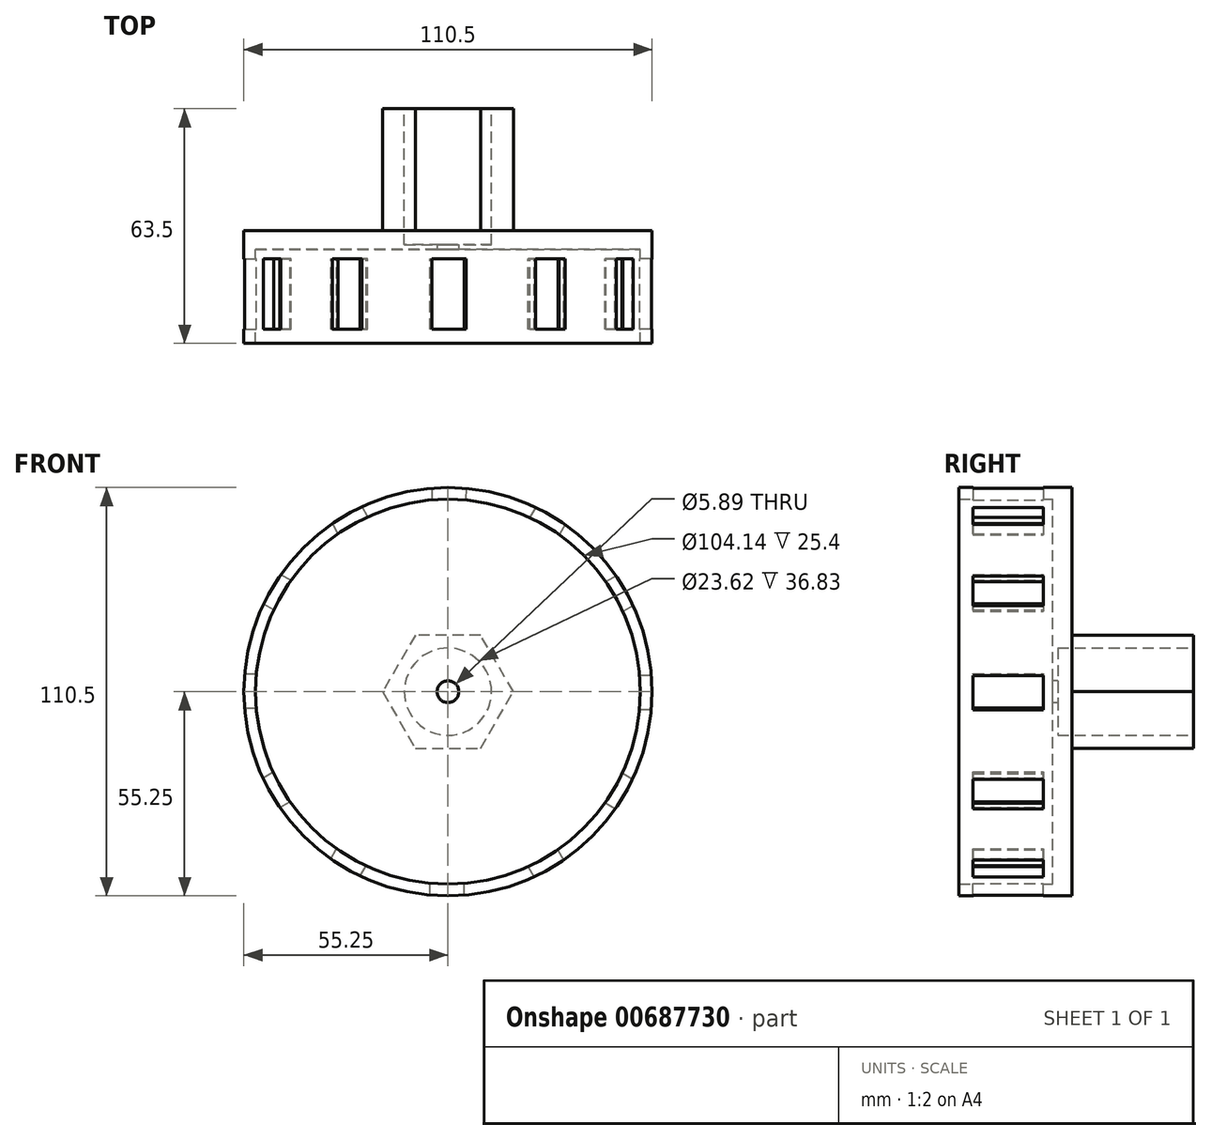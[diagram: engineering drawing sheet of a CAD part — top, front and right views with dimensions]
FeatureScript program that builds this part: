
annotation { "Feature Type Name" : "Feature", "Feature Type Description" : "" }
export const myFeature = defineFeature(function(context is Context, id is Id, definition is map)
    precondition{}
    {
        {
            var Q0;
            Q0=qCreatedBy(makeId("Front.planeOp"),FACE);
            var sketch = newSketch(context, id + "F0", { "sketchPlane" : qUnion([Q0])});
            skCircle(sketch, "E0", {"center": v(0, 0) * mm, "radius": 52.07 * mm});
            skCircle(sketch, "E1", {"center": v(0, 0) * mm, "radius": 55.24 * mm});
            skSolve(sketch);
        }
        {
            var Q0;
            Q0=makeQuery(id+"F0.imprint","IMPRINT",FACE,{"disambiguationData":[TD([[makeQuery(id+"F0.imprint","IMPRINT",EDGE,{"derivedFrom":sQuery(id+"F0.wireOp",EDGE,"E0")}),1.0]])]});
            extrude(context, id + "F1", {"entities" : qUnion([Q0]), "depth" : 5.08 * mm, "offsetDistance" : 25.4 * mm});
        }
        {
            var Q0;
            Q0=makeQuery(id+"F0.imprint","IMPRINT",FACE,{"disambiguationData":[TD([[makeQuery(id+"F0.imprint","IMPRINT",EDGE,{"derivedFrom":sQuery(id+"F0.wireOp",EDGE,"E0")}),-1.0]])]});
            extrude(context, id + "F2", {"entities" : qUnion([Q0]), "operationType" : NewBodyOperationType.ADD, "depth" : 30.48 * mm, "offsetDistance" : 25.4 * mm});
        }
        {
            var Q0;
            Q0=makeQuery(id+"F1.opExtrude","CAP_FACE",FACE,{"disambiguationData":[OSD([sQuery(id+"F0.wireOp",EDGE,"E0")])],"isStart":false});
            var sketch = newSketch(context, id + "F3", { "sketchPlane" : qUnion([Q0])});
            skCircle(sketch, "E2.cCircle", {"center": v(0, 0) * mm, "radius": 17.26 * mm, "construction": true});
            skLineSegment(sketch, "E2.0", {"start": v(12.58, -12.7) * mm, "end": v(4.55, -17.28) * mm});
            skLineSegment(sketch, "E2.1", {"start": v(4.55, -17.28) * mm, "end": v(-4.7, -17.24) * mm});
            skLineSegment(sketch, "E2.2", {"start": v(-4.7, -17.24) * mm, "end": v(-12.7, -12.58) * mm});
            skLineSegment(sketch, "E2.3", {"start": v(-12.7, -12.58) * mm, "end": v(-17.28, -4.55) * mm});
            skLineSegment(sketch, "E2.4", {"start": v(-17.28, -4.55) * mm, "end": v(-17.24, 4.7) * mm});
            skLineSegment(sketch, "E2.5", {"start": v(-17.24, 4.7) * mm, "end": v(-12.58, 12.7) * mm});
            skLineSegment(sketch, "E2.6", {"start": v(-12.58, 12.7) * mm, "end": v(-4.55, 17.28) * mm});
            skLineSegment(sketch, "E2.7", {"start": v(-4.55, 17.28) * mm, "end": v(4.7, 17.24) * mm});
            skLineSegment(sketch, "E2.8", {"start": v(4.7, 17.24) * mm, "end": v(12.7, 12.58) * mm});
            skLineSegment(sketch, "E2.9", {"start": v(12.7, 12.58) * mm, "end": v(17.28, 4.55) * mm});
            skLineSegment(sketch, "E2.10", {"start": v(17.28, 4.55) * mm, "end": v(17.24, -4.7) * mm});
            skLineSegment(sketch, "E2.11", {"start": v(17.24, -4.7) * mm, "end": v(12.58, -12.7) * mm});
            skPoint(sketch, "E2.0.midPoint", {"position": v(8.57, -14.99) * mm});
            skSolve(sketch);
        }
        {
            var Q0;
            Q0=makeQuery(id+"F3.imprint","IMPRINT",FACE,{"disambiguationData":[TD([[makeQuery(id+"F3.imprint","IMPRINT",EDGE,{"derivedFrom":sQuery(id+"F3.wireOp",EDGE,"E2.0")}),-1.0]])]});
            extrude(context, id + "F4", {"entities" : qUnion([Q0]), "operationType" : NewBodyOperationType.ADD, "depth" : 21.59 * mm, "offsetDistance" : 25.4 * mm});
        }
        {
            var Q0;
            Q0=makeQuery(id+"F4.opExtrude","SWEPT_FACE",FACE,{"disambiguationData":[OSD([sQuery(id+"F3.wireOp",EDGE,"E2.8")])]});
            var sketch = newSketch(context, id + "F5", { "sketchPlane" : qUnion([Q0])});
            skLineSegment(sketch, "E3", {"start": v(-4.63, -7.62) * mm, "end": v(4.63, -7.62) * mm});
            skSolve(sketch);
        }
        {
            var Q0;
            {var subQ0=sQuery(id+"F5.wireOp",EDGE,"E3");Q0=makeQuery(id+"F5.imprint","IMPRINT",FACE,{"disambiguationData":[TD([[makeQuery(id+"F5.imprint","IMPRINT",EDGE,{"derivedFrom":subQ0}),-1.0]])]});}
            extrude(context, id + "F6", {"entities" : qUnion([Q0]), "operationType" : NewBodyOperationType.REMOVE, "depth" : 50.8 * mm, "offsetDistance" : 25.4 * mm});
        }
        {
            var Q0;
            Q0=makeQuery(id+"F4.opExtrude","SWEPT_FACE",FACE,{"disambiguationData":[OSD([sQuery(id+"F3.wireOp",EDGE,"E2.7")])]});
            var sketch = newSketch(context, id + "F7", { "sketchPlane" : qUnion([Q0])});
            skLineSegment(sketch, "E4", {"start": v(4.63, -7.62) * mm, "end": v(-4.63, -7.62) * mm});
            skSolve(sketch);
        }
        {
            var Q0;
            {var subQ0=sQuery(id+"F7.wireOp",EDGE,"E4");Q0=makeQuery(id+"F7.imprint","IMPRINT",FACE,{"disambiguationData":[TD([[makeQuery(id+"F7.imprint","IMPRINT",EDGE,{"derivedFrom":subQ0}),1.0]])]});}
            extrude(context, id + "F8", {"entities" : qUnion([Q0]), "operationType" : NewBodyOperationType.REMOVE, "depth" : 50.8 * mm, "offsetDistance" : 25.4 * mm});
        }
        {
            var Q0;
            Q0=makeQuery(id+"F4.opExtrude","SWEPT_FACE",FACE,{"disambiguationData":[OSD([sQuery(id+"F3.wireOp",EDGE,"E2.6")])]});
            var sketch = newSketch(context, id + "F9", { "sketchPlane" : qUnion([Q0])});
            skLineSegment(sketch, "E5", {"start": v(4.63, -7.62) * mm, "end": v(-4.63, -7.62) * mm});
            skSolve(sketch);
        }
        {
            var Q0;
            {var subQ0=sQuery(id+"F9.wireOp",EDGE,"E5");Q0=makeQuery(id+"F9.imprint","IMPRINT",FACE,{"disambiguationData":[TD([[makeQuery(id+"F9.imprint","IMPRINT",EDGE,{"derivedFrom":subQ0}),1.0]])]});}
            extrude(context, id + "F10", {"entities" : qUnion([Q0]), "operationType" : NewBodyOperationType.REMOVE, "depth" : 50.8 * mm, "offsetDistance" : 25.4 * mm});
        }
        {
            var Q0;
            Q0=makeQuery(id+"F4.opExtrude","SWEPT_FACE",FACE,{"disambiguationData":[OSD([sQuery(id+"F3.wireOp",EDGE,"E2.5")])]});
            var sketch = newSketch(context, id + "F11", { "sketchPlane" : qUnion([Q0])});
            skLineSegment(sketch, "E6", {"start": v(7.62, 4.63) * mm, "end": v(7.62, -4.63) * mm});
            skSolve(sketch);
        }
        {
            var Q0;
            {var subQ0=sQuery(id+"F11.wireOp",EDGE,"E6");Q0=makeQuery(id+"F11.imprint","IMPRINT",FACE,{"disambiguationData":[TD([[makeQuery(id+"F11.imprint","IMPRINT",EDGE,{"derivedFrom":subQ0}),1.0]])]});}
            extrude(context, id + "F12", {"entities" : qUnion([Q0]), "operationType" : NewBodyOperationType.REMOVE, "depth" : 50.8 * mm, "offsetDistance" : 25.4 * mm});
        }
        {
            var Q0;
            Q0=makeQuery(id+"F4.opExtrude","SWEPT_FACE",FACE,{"disambiguationData":[OSD([sQuery(id+"F3.wireOp",EDGE,"E2.4")])]});
            var sketch = newSketch(context, id + "F13", { "sketchPlane" : qUnion([Q0])});
            skLineSegment(sketch, "E7", {"start": v(7.62, 4.63) * mm, "end": v(7.62, -4.63) * mm});
            skSolve(sketch);
        }
        {
            var Q0;
            {var subQ0=sQuery(id+"F13.wireOp",EDGE,"E7");Q0=makeQuery(id+"F13.imprint","IMPRINT",FACE,{"disambiguationData":[TD([[makeQuery(id+"F13.imprint","IMPRINT",EDGE,{"derivedFrom":subQ0}),1.0]])]});}
            extrude(context, id + "F14", {"entities" : qUnion([Q0]), "operationType" : NewBodyOperationType.REMOVE, "depth" : 50.8 * mm, "offsetDistance" : 25.4 * mm});
        }
        {
            var Q0;
            Q0=makeQuery(id+"F4.opExtrude","SWEPT_FACE",FACE,{"disambiguationData":[OSD([sQuery(id+"F3.wireOp",EDGE,"E2.3")])]});
            var sketch = newSketch(context, id + "F15", { "sketchPlane" : qUnion([Q0])});
            skLineSegment(sketch, "E8", {"start": v(7.62, 4.63) * mm, "end": v(7.62, -4.63) * mm});
            skSolve(sketch);
        }
        {
            var Q0;
            {var subQ0=sQuery(id+"F15.wireOp",EDGE,"E8");Q0=makeQuery(id+"F15.imprint","IMPRINT",FACE,{"disambiguationData":[TD([[makeQuery(id+"F15.imprint","IMPRINT",EDGE,{"derivedFrom":subQ0}),1.0]])]});}
            extrude(context, id + "F16", {"entities" : qUnion([Q0]), "operationType" : NewBodyOperationType.REMOVE, "depth" : 50.8 * mm, "offsetDistance" : 25.4 * mm});
        }
        {
            var Q0;
            Q0=makeQuery(id+"F4.opExtrude","SWEPT_FACE",FACE,{"disambiguationData":[OSD([sQuery(id+"F3.wireOp",EDGE,"E2.2")])]});
            var sketch = newSketch(context, id + "F17", { "sketchPlane" : qUnion([Q0])});
            skLineSegment(sketch, "E9", {"start": v(-4.63, 7.62) * mm, "end": v(4.63, 7.62) * mm});
            skSolve(sketch);
        }
        {
            var Q0;
            {var subQ0=sQuery(id+"F17.wireOp",EDGE,"E9");Q0=makeQuery(id+"F17.imprint","IMPRINT",FACE,{"disambiguationData":[TD([[makeQuery(id+"F17.imprint","IMPRINT",EDGE,{"derivedFrom":subQ0}),1.0]])]});}
            extrude(context, id + "F18", {"entities" : qUnion([Q0]), "operationType" : NewBodyOperationType.REMOVE, "depth" : 50.8 * mm, "offsetDistance" : 25.4 * mm});
        }
        {
            var Q0;
            Q0=makeQuery(id+"F4.opExtrude","SWEPT_FACE",FACE,{"disambiguationData":[OSD([sQuery(id+"F3.wireOp",EDGE,"E2.1")])]});
            var sketch = newSketch(context, id + "F19", { "sketchPlane" : qUnion([Q0])});
            skLineSegment(sketch, "E10", {"start": v(-4.63, 7.62) * mm, "end": v(4.63, 7.62) * mm});
            skSolve(sketch);
        }
        {
            var Q0;
            {var subQ0=sQuery(id+"F19.wireOp",EDGE,"E10");Q0=makeQuery(id+"F19.imprint","IMPRINT",FACE,{"disambiguationData":[TD([[makeQuery(id+"F19.imprint","IMPRINT",EDGE,{"derivedFrom":subQ0}),1.0]])]});}
            extrude(context, id + "F20", {"entities" : qUnion([Q0]), "operationType" : NewBodyOperationType.REMOVE, "depth" : 50.8 * mm, "offsetDistance" : 25.4 * mm});
        }
        {
            var Q0;
            Q0=makeQuery(id+"F4.opExtrude","SWEPT_FACE",FACE,{"disambiguationData":[OSD([sQuery(id+"F3.wireOp",EDGE,"E2.0")])]});
            var sketch = newSketch(context, id + "F21", { "sketchPlane" : qUnion([Q0])});
            skLineSegment(sketch, "E11", {"start": v(-4.63, 7.62) * mm, "end": v(4.63, 7.62) * mm});
            skSolve(sketch);
        }
        {
            var Q0;
            {var subQ0=sQuery(id+"F21.wireOp",EDGE,"E11");Q0=makeQuery(id+"F21.imprint","IMPRINT",FACE,{"disambiguationData":[TD([[makeQuery(id+"F21.imprint","IMPRINT",EDGE,{"derivedFrom":subQ0}),1.0]])]});}
            extrude(context, id + "F22", {"entities" : qUnion([Q0]), "operationType" : NewBodyOperationType.REMOVE, "depth" : 50.8 * mm, "offsetDistance" : 25.4 * mm});
        }
        {
            var Q0;
            Q0=makeQuery(id+"F4.opExtrude","SWEPT_FACE",FACE,{"disambiguationData":[OSD([sQuery(id+"F3.wireOp",EDGE,"E2.11")])]});
            var sketch = newSketch(context, id + "F23", { "sketchPlane" : qUnion([Q0])});
            skLineSegment(sketch, "E12", {"start": v(-7.62, -4.63) * mm, "end": v(-7.62, 4.63) * mm});
            skSolve(sketch);
        }
        {
            var Q0;
            {var subQ0=sQuery(id+"F23.wireOp",EDGE,"E12");Q0=makeQuery(id+"F23.imprint","IMPRINT",FACE,{"disambiguationData":[TD([[makeQuery(id+"F23.imprint","IMPRINT",EDGE,{"derivedFrom":subQ0}),1.0]])]});}
            extrude(context, id + "F24", {"entities" : qUnion([Q0]), "operationType" : NewBodyOperationType.REMOVE, "depth" : 50.8 * mm, "offsetDistance" : 25.4 * mm});
        }
        {
            var Q0;
            Q0=makeQuery(id+"F4.opExtrude","SWEPT_FACE",FACE,{"disambiguationData":[OSD([sQuery(id+"F3.wireOp",EDGE,"E2.10")])]});
            var sketch = newSketch(context, id + "F25", { "sketchPlane" : qUnion([Q0])});
            skLineSegment(sketch, "E13", {"start": v(-7.62, 4.63) * mm, "end": v(-7.62, -4.63) * mm});
            skSolve(sketch);
        }
        {
            var Q0;
            {var subQ0=sQuery(id+"F25.wireOp",EDGE,"E13");Q0=makeQuery(id+"F25.imprint","IMPRINT",FACE,{"disambiguationData":[TD([[makeQuery(id+"F25.imprint","IMPRINT",EDGE,{"derivedFrom":subQ0}),-1.0]])]});}
            extrude(context, id + "F26", {"entities" : qUnion([Q0]), "operationType" : NewBodyOperationType.REMOVE, "depth" : 50.8 * mm, "offsetDistance" : 25.4 * mm});
        }
        {
            var Q0;
            Q0=makeQuery(id+"F4.opExtrude","SWEPT_FACE",FACE,{"disambiguationData":[OSD([sQuery(id+"F3.wireOp",EDGE,"E2.9")])]});
            var sketch = newSketch(context, id + "F27", { "sketchPlane" : qUnion([Q0])});
            skLineSegment(sketch, "E14", {"start": v(-7.62, 4.63) * mm, "end": v(-7.62, -4.63) * mm});
            skSolve(sketch);
        }
        {
            var Q0;
            {var subQ0=sQuery(id+"F27.wireOp",EDGE,"E14");Q0=makeQuery(id+"F27.imprint","IMPRINT",FACE,{"disambiguationData":[TD([[makeQuery(id+"F27.imprint","IMPRINT",EDGE,{"derivedFrom":subQ0}),-1.0]])]});}
            extrude(context, id + "F28", {"entities" : qUnion([Q0]), "operationType" : NewBodyOperationType.REMOVE, "depth" : 50.8 * mm, "offsetDistance" : 25.4 * mm});
        }
        {
            var Q0;
            Q0=makeQuery(id+"F0.imprint","IMPRINT",FACE,{"disambiguationData":[TD([[makeQuery(id+"F0.imprint","IMPRINT",EDGE,{"derivedFrom":sQuery(id+"F0.wireOp",EDGE,"E0")}),1.0]])]});
            var sketch = newSketch(context, id + "F29", { "sketchPlane" : qUnion([Q0])});
            skLineSegment(sketch, "E15.bottom", {"start": v(20.4, 19.07) * mm, "end": v(-20.24, 19.07) * mm});
            skLineSegment(sketch, "E15.top", {"start": v(20.4, -19.03) * mm, "end": v(-20.24, -19.03) * mm});
            skLineSegment(sketch, "E15.left", {"start": v(20.4, 19.07) * mm, "end": v(20.4, -19.03) * mm});
            skLineSegment(sketch, "E15.right", {"start": v(-20.24, 19.07) * mm, "end": v(-20.24, -19.03) * mm});
            skSolve(sketch);
        }
        {
            var Q0;
            Q0=makeQuery(id+"F29.imprint","IMPRINT",FACE,{"disambiguationData":[TD([[makeQuery(id+"F29.imprint","IMPRINT",EDGE,{"derivedFrom":sQuery(id+"F29.wireOp",EDGE,"E15.bottom")}),1.0]])]});
            extrude(context, id + "F30", {"entities" : qUnion([Q0]), "operationType" : NewBodyOperationType.ADD, "oppositeDirection" : true, "depth" : 33.02 * mm, "offsetDistance" : 25.4 * mm});
        }
        {
            var Q0;
            Q0=makeQuery(id+"F4.opExtrude","CAP_FACE",FACE,{"disambiguationData":[OSD([sQuery(id+"F3.wireOp",EDGE,"E2.0"),sQuery(id+"F3.wireOp",EDGE,"E2.1"),sQuery(id+"F3.wireOp",EDGE,"E2.2"),sQuery(id+"F3.wireOp",EDGE,"E2.3"),sQuery(id+"F3.wireOp",EDGE,"E2.4"),sQuery(id+"F3.wireOp",EDGE,"E2.5"),sQuery(id+"F3.wireOp",EDGE,"E2.6"),sQuery(id+"F3.wireOp",EDGE,"E2.7"),sQuery(id+"F3.wireOp",EDGE,"E2.8"),sQuery(id+"F3.wireOp",EDGE,"E2.9"),sQuery(id+"F3.wireOp",EDGE,"E2.10"),sQuery(id+"F3.wireOp",EDGE,"E2.11")])],"isStart":false});
            extrude(context, id + "F31", {"entities" : qUnion([Q0]), "operationType" : NewBodyOperationType.REMOVE, "oppositeDirection" : true, "depth" : 21.59 * mm, "offsetDistance" : 25.4 * mm});
        }
        {
            var Q0;
            Q0=makeQuery(id+"F30.opExtrude","CAP_FACE",FACE,{"disambiguationData":[OSD([sQuery(id+"F29.wireOp",EDGE,"E15.bottom"),sQuery(id+"F29.wireOp",EDGE,"E15.top"),sQuery(id+"F29.wireOp",EDGE,"E15.left"),sQuery(id+"F29.wireOp",EDGE,"E15.right")])],"isStart":false});
            var sketch = newSketch(context, id + "F32", { "sketchPlane" : qUnion([Q0])});
            skCircle(sketch, "E16", {"center": v(0, 0) * mm, "radius": 11.81 * mm});
            skSolve(sketch);
        }
        {
            var Q0;
            Q0=makeQuery(id+"F31.boolean.opBoolean","MERGE",FACE,{"derivedFrom":[makeQuery(id+"F1.opExtrude","CAP_FACE",FACE,{"disambiguationData":[OSD([sQuery(id+"F0.wireOp",EDGE,"E0")])],"isStart":false}),makeQuery(id+"F31.opExtrude","CAP_FACE",FACE,{"disambiguationData":[OSD([sQuery(id+"F3.wireOp",EDGE,"E2.0"),sQuery(id+"F3.wireOp",EDGE,"E2.1"),sQuery(id+"F3.wireOp",EDGE,"E2.2"),sQuery(id+"F3.wireOp",EDGE,"E2.3"),sQuery(id+"F3.wireOp",EDGE,"E2.4"),sQuery(id+"F3.wireOp",EDGE,"E2.5"),sQuery(id+"F3.wireOp",EDGE,"E2.6"),sQuery(id+"F3.wireOp",EDGE,"E2.7"),sQuery(id+"F3.wireOp",EDGE,"E2.8"),sQuery(id+"F3.wireOp",EDGE,"E2.9"),sQuery(id+"F3.wireOp",EDGE,"E2.10"),sQuery(id+"F3.wireOp",EDGE,"E2.11")])],"isStart":false})]});
            var sketch = newSketch(context, id + "F33", { "sketchPlane" : qUnion([Q0])});
            skCircle(sketch, "E17", {"center": v(0, 0) * mm, "radius": 2.95 * mm});
            skSolve(sketch);
        }
        {
            var Q0;
            Q0=makeQuery(id+"F33.imprint","IMPRINT",FACE,{"disambiguationData":[TD([[makeQuery(id+"F33.imprint","IMPRINT",EDGE,{"derivedFrom":sQuery(id+"F33.wireOp",EDGE,"E17")}),1.0]])]});
            extrude(context, id + "F34", {"entities" : qUnion([Q0]), "operationType" : NewBodyOperationType.REMOVE, "oppositeDirection" : true, "depth" : 1.63 * mm, "offsetDistance" : 25.4 * mm});
        }
        {
            var Q0;
            Q0=makeQuery(id+"F32.imprint","IMPRINT",FACE,{"disambiguationData":[TD([[makeQuery(id+"F32.imprint","IMPRINT",EDGE,{"derivedFrom":sQuery(id+"F32.wireOp",EDGE,"E16")}),1.0]])]});
            extrude(context, id + "F35", {"entities" : qUnion([Q0]), "operationType" : NewBodyOperationType.REMOVE, "oppositeDirection" : true, "depth" : 36.83 * mm, "offsetDistance" : 25.4 * mm});
        }
        {
            var Q0;
            Q0=makeQuery(id+"F30.opExtrude","CAP_FACE",FACE,{"disambiguationData":[OSD([sQuery(id+"F29.wireOp",EDGE,"E15.bottom"),sQuery(id+"F29.wireOp",EDGE,"E15.top"),sQuery(id+"F29.wireOp",EDGE,"E15.left"),sQuery(id+"F29.wireOp",EDGE,"E15.right")])],"isStart":false});
            var sketch = newSketch(context, id + "F36", { "sketchPlane" : qUnion([Q0])});
            skCircle(sketch, "E18.cCircle", {"center": v(0, 0) * mm, "radius": 15.31 * mm, "construction": true});
            skLineSegment(sketch, "E18.0", {"start": v(8.84, -15.31) * mm, "end": v(-8.84, -15.31) * mm});
            skLineSegment(sketch, "E18.1", {"start": v(-8.84, -15.31) * mm, "end": v(-17.68, 0) * mm});
            skLineSegment(sketch, "E18.2", {"start": v(-17.68, 0) * mm, "end": v(-8.84, 15.31) * mm});
            skLineSegment(sketch, "E18.3", {"start": v(-8.84, 15.31) * mm, "end": v(8.84, 15.31) * mm});
            skLineSegment(sketch, "E18.4", {"start": v(8.84, 15.31) * mm, "end": v(17.68, 0) * mm});
            skLineSegment(sketch, "E18.5", {"start": v(17.68, 0) * mm, "end": v(8.84, -15.31) * mm});
            skPoint(sketch, "E18.0.midPoint", {"position": v(0, -15.31) * mm});
            skSolve(sketch);
        }
        {
            var Q0;
            Q0=makeQuery(id+"F36.imprint","IMPRINT",FACE,{"disambiguationData":[TD([[makeQuery(id+"F36.imprint","IMPRINT",EDGE,{"derivedFrom":sQuery(id+"F36.wireOp",EDGE,"E18.0")}),1.0]])]});
            extrude(context, id + "F37", {"entities" : qUnion([Q0]), "operationType" : NewBodyOperationType.REMOVE, "oppositeDirection" : true, "depth" : 33.02 * mm, "offsetDistance" : 25.4 * mm});
        }
    });
